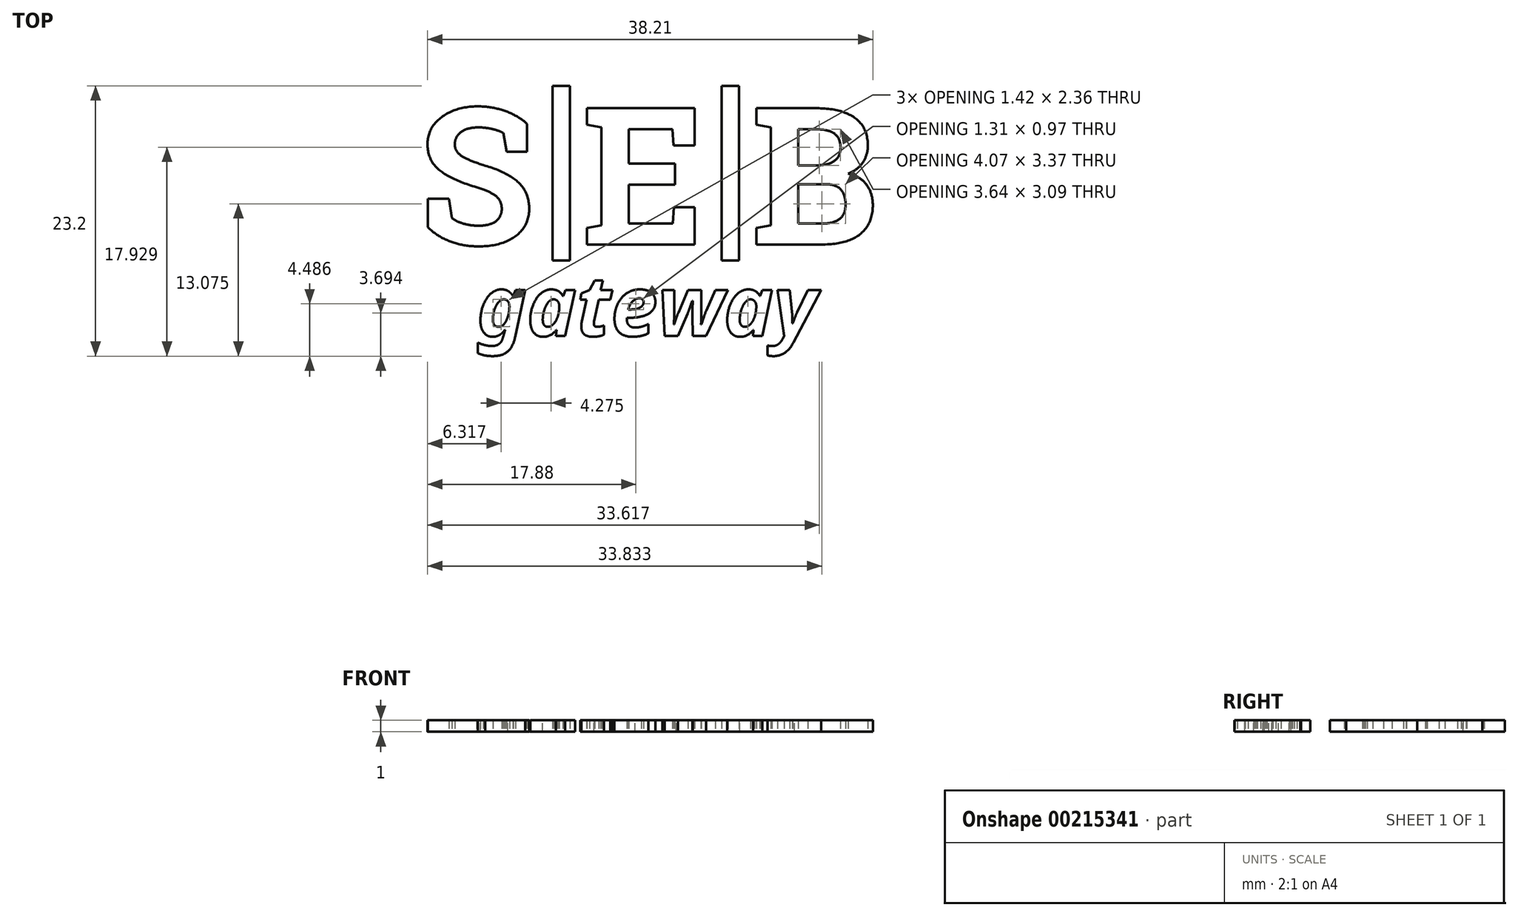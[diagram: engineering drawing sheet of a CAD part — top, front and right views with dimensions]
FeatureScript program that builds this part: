
annotation { "Feature Type Name" : "Feature", "Feature Type Description" : "" }
export const myFeature = defineFeature(function(context is Context, id is Id, definition is map)
    precondition{}
    {
        {
            var Q0;
            Q0=qCreatedBy(makeId("Top.planeOp"),FACE);
            var sketch = newSketch(context, id + "F0", { "sketchPlane" : qUnion([Q0])});
            skText(sketch, "E0", { "text": "S E B", "fontName": "RobotoSlab-Bold.ttf"});
            skText(sketch, "E1", { "text": "gateway", "fontName": "NotoSans-BoldItalic.ttf"});
            skLineSegment(sketch, "E2.bottom", {"start": v(-0.03, 8.6) * mm, "end": v(1.47, 8.6) * mm});
            skLineSegment(sketch, "E2.top", {"start": v(-0.03, -6.4) * mm, "end": v(1.47, -6.4) * mm});
            skLineSegment(sketch, "E2.left", {"start": v(-0.03, 8.6) * mm, "end": v(-0.03, -6.4) * mm});
            skLineSegment(sketch, "E2.right", {"start": v(1.47, 8.6) * mm, "end": v(1.47, -6.4) * mm});
            skLineSegment(sketch, "E3.bottom", {"start": v(14.47, 8.6) * mm, "end": v(15.97, 8.6) * mm});
            skLineSegment(sketch, "E3.top", {"start": v(14.47, -6.4) * mm, "end": v(15.97, -6.4) * mm});
            skLineSegment(sketch, "E3.left", {"start": v(14.47, 8.6) * mm, "end": v(14.47, -6.4) * mm});
            skLineSegment(sketch, "E3.right", {"start": v(15.97, 8.6) * mm, "end": v(15.97, -6.4) * mm});
            const initialGuessF0  = {"E0": [-0.01153, -0.005, 1, 0, 0.01184], "E1": [-0.00653, -0.01286, 1, 0, 0.00518]};
            skSetInitialGuess(sketch, initialGuessF0);
            skSolve(sketch);
        }
        {
            var Q0;
            Q0 = qSketchRegion(id + "F0", true);
            extrude(context, id + "F1", {"entities" : qUnion([Q0]), "depth" : 1 * mm});
        }
    });
